# Revit family: DCST_Счетчик водяной комбинированный_СТВК 1
name_source: partatom
category: Арматура трубопроводов
units: mm (PartAtom-declared; Revit-internal decimal feet)

## family parameters
Всегда вертикально = Да
На основе рабочей плоскости = Нет
Общий = Нет
При загрузке вырезать с полостями = Нет
Размер круглого соединителя = Использовать диаметр
Тип детали = Вставляется

## types (3) — shared parameters
ADSK_Единица измерения = шт.
ADSK_Завод-изготовитель = Декаст
ADSK_Количество = 1
ADSK_Материал = Декаст_Корпус счетчика синий
LT = СТВК 1
URL = https://www.decast.com
ИПД_ДГ2 = ♦ : импульсный выход (геркон)
ИПД_Нет = ♦ : нет
Изготовитель = Декаст

## per-type parameters (varying)
| type | ADSK_Диаметр условный | D1 | D2 | D3 | D4 | D5 | D6 | L1 | L2 | L3 | L4 | L5 | L6 | f | h | s | t | Геометрия50 | Геометрия80 | Диаметр условного прохода | Монтажная длина | УГО_Высота | УГО_Длина | УГО_Длина линии |
| СТВК 1 100 | 100 мм | 116 мм | 95.6 мм | 112.6 мм | 130 мм | 117.2 мм | 133.4 мм | 57 мм | 10 мм | 115 мм | 16 мм | 100 мм | 11 мм | 17 мм | 57 мм | 40 мм | 105 мм | Нет | Да | 100 мм | 370 мм | 168 мм | 336 мм | 17 мм |
| СТВК 1 80 | 80 мм | 116 мм | 95.6 мм | 112.6 мм | 130 мм | 117.2 мм | 133.4 мм | 57 мм | 10 мм | 115 мм | 16 мм | 100 мм | 11 мм | 16 мм | 57 мм | 40 мм | 95 мм | Нет | Да | 80 мм | 370 мм | 169 мм | 338 мм | 16 мм |
| СТВК 1 50 | 50 мм | 124 мм | 94 мм | 94 мм | 94 мм | 80 мм | 112 мм | 16.5 мм | 37.1 мм | 37.1 мм | 37.1 мм | 37.1 мм | 37.1 мм | 13 мм | 51 мм | 16 мм | 75 мм | Да | Нет | 50 мм | 270 мм | 122 мм | 244 мм | 13 мм |
